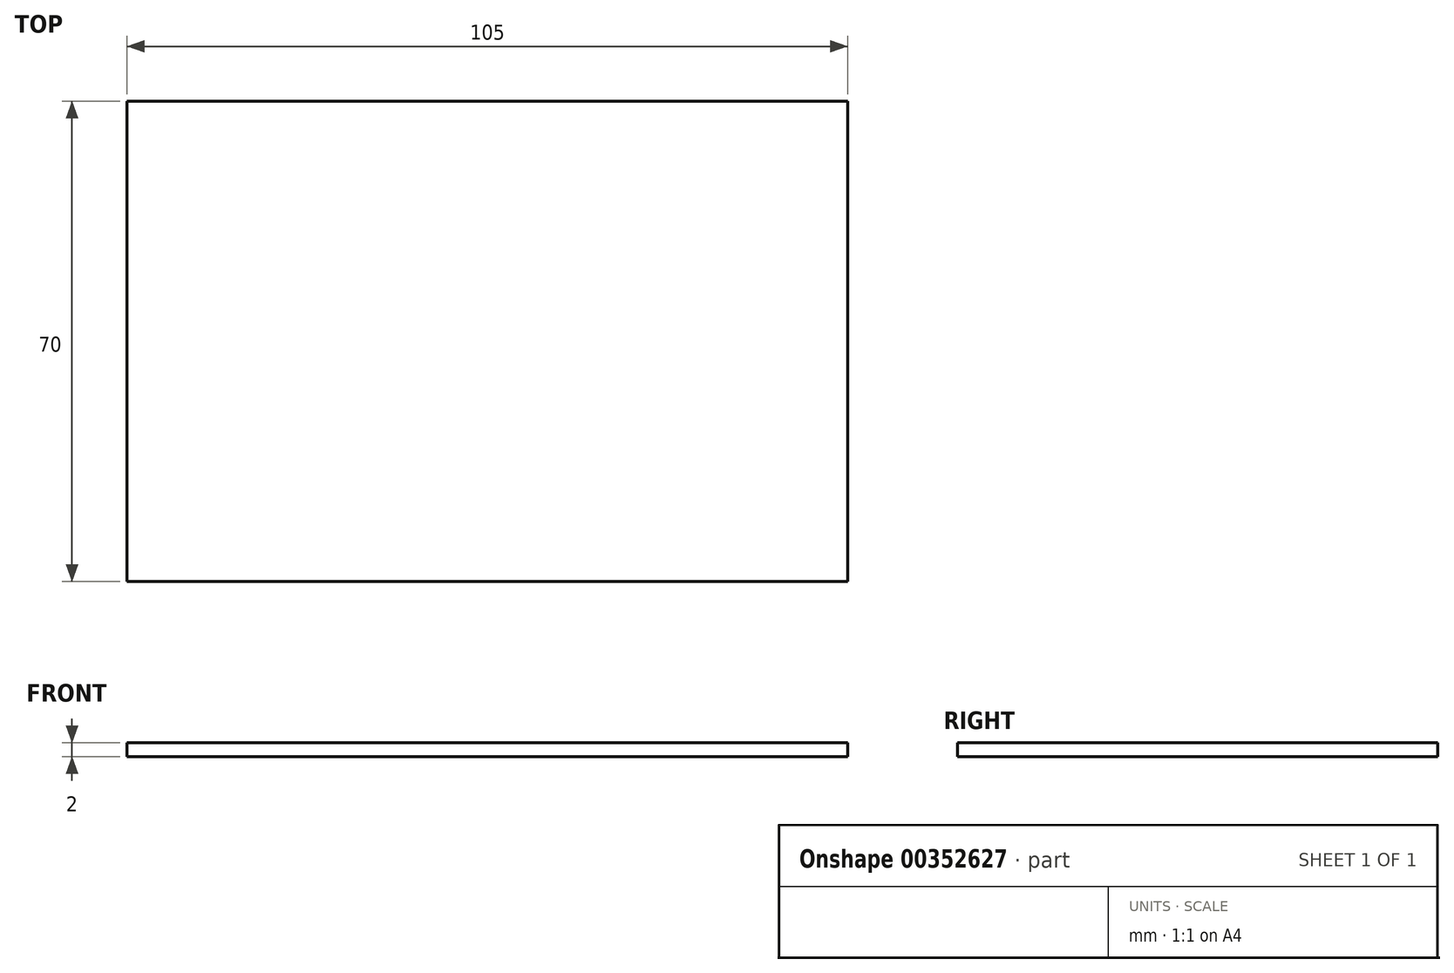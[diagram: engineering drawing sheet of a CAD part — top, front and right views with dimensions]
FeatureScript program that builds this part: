
annotation { "Feature Type Name" : "Feature", "Feature Type Description" : "" }
export const myFeature = defineFeature(function(context is Context, id is Id, definition is map)
    precondition{}
    {
        {
            var Q0;
            Q0=qCreatedBy(makeId("Top.planeOp"),FACE);
            var sketch = newSketch(context, id + "F0", { "sketchPlane" : qUnion([Q0])});
            skLineSegment(sketch, "E0.bottom", {"start": v(-52.5, 35) * mm, "end": v(52.5, 35) * mm});
            skLineSegment(sketch, "E0.top", {"start": v(-52.5, -35) * mm, "end": v(52.5, -35) * mm});
            skLineSegment(sketch, "E0.left", {"start": v(-52.5, 35) * mm, "end": v(-52.5, -35) * mm});
            skLineSegment(sketch, "E0.right", {"start": v(52.5, 35) * mm, "end": v(52.5, -35) * mm});
            skPoint(sketch, "E0.middle", {"position": v(0, 0) * mm});
            skSolve(sketch);
        }
        {
            var Q0;
            Q0 = qSketchRegion(id + "F0", true);
            extrude(context, id + "F1", {"entities" : qUnion([Q0]), "depth" : 2 * mm});
        }
    });
